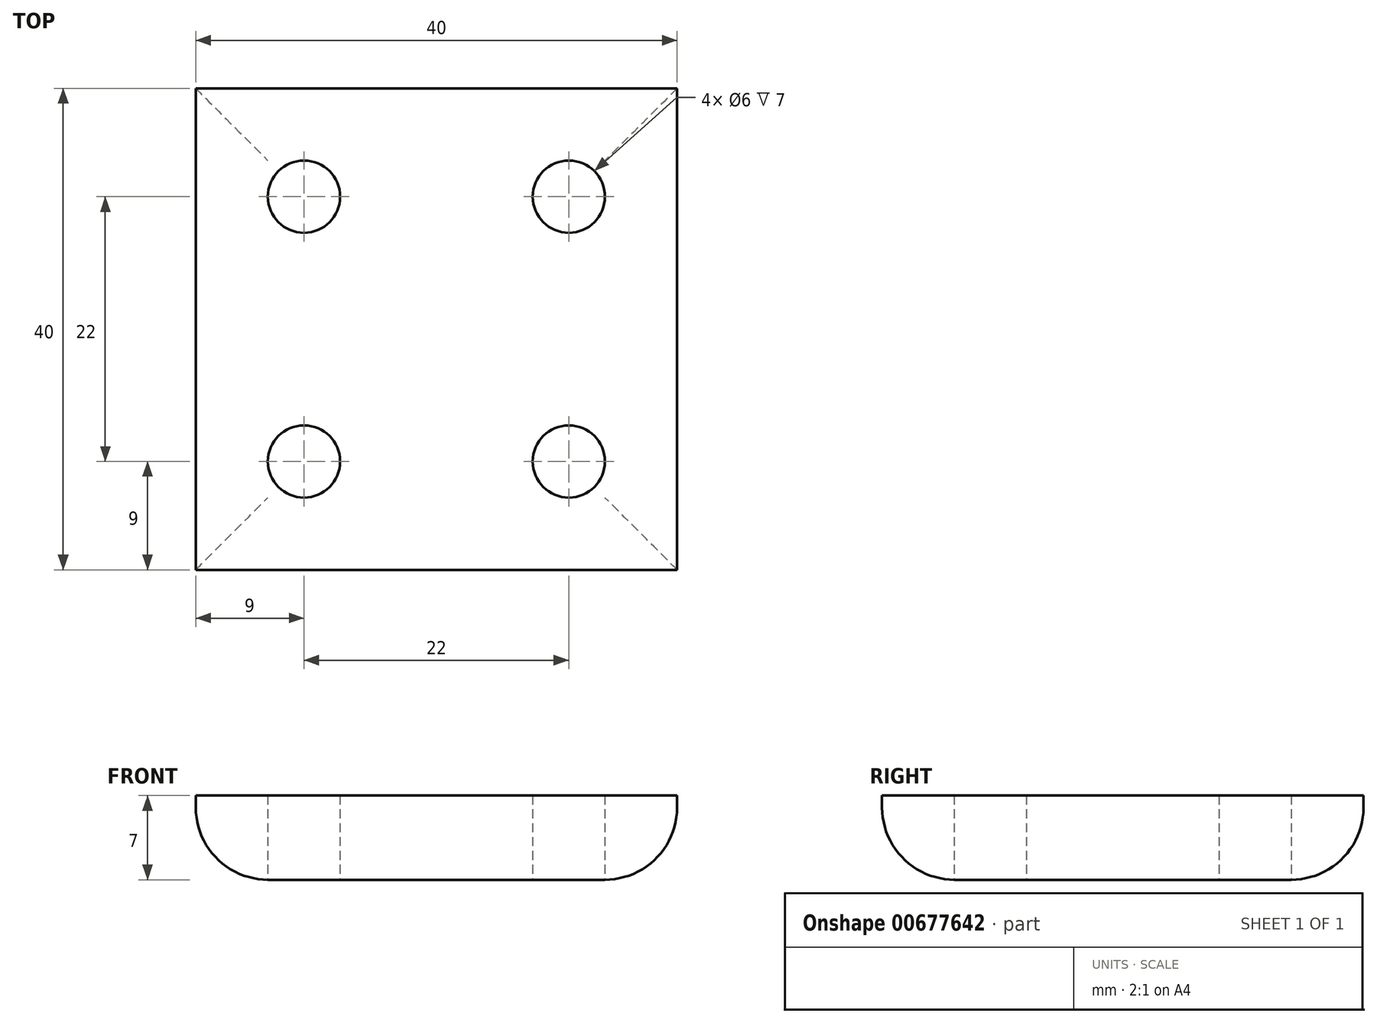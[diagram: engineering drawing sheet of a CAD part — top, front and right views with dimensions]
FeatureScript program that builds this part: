
annotation { "Feature Type Name" : "Feature", "Feature Type Description" : "" }
export const myFeature = defineFeature(function(context is Context, id is Id, definition is map)
    precondition{}
    {
        {
            var Q0;
            Q0=qCreatedBy(makeId("Top.planeOp"),FACE);
            var sketch = newSketch(context, id + "F0", { "sketchPlane" : qUnion([Q0])});
            skLineSegment(sketch, "E0.bottom", {"start": v(0, 0) * mm, "end": v(40, 0) * mm});
            skLineSegment(sketch, "E0.top", {"start": v(0, 40) * mm, "end": v(40, 40) * mm});
            skLineSegment(sketch, "E0.left", {"start": v(0, 0) * mm, "end": v(0, 40) * mm});
            skLineSegment(sketch, "E0.right", {"start": v(40, 0) * mm, "end": v(40, 40) * mm});
            skCircle(sketch, "E1", {"center": v(31, 9) * mm, "radius": 3 * mm});
            skCircle(sketch, "E2.0.1.0", {"center": v(31, 31) * mm, "radius": 3 * mm});
            skCircle(sketch, "E2.1.0.0", {"center": v(9, 9) * mm, "radius": 3 * mm});
            skCircle(sketch, "E2.1.1.0", {"center": v(9, 31) * mm, "radius": 3 * mm});
            skLineSegment(sketch, "E2.direction1", {"start": v(31, 9) * mm, "end": v(9, 9) * mm, "construction": true});
            skLineSegment(sketch, "E2.direction2", {"start": v(31, 9) * mm, "end": v(31, 31) * mm, "construction": true});
            skSolve(sketch);
        }
        {
            var Q0;
            Q0=makeQuery(id+"F0.imprint","IMPRINT",FACE,{"disambiguationData":[TD([[makeQuery(id+"F0.imprint","IMPRINT",EDGE,{"derivedFrom":sQuery(id+"F0.wireOp",EDGE,"E0.bottom")}),1.0]])]});
            extrude(context, id + "F1", {"entities" : qUnion([Q0]), "depth" : 7 * mm, "offsetDistance" : 25 * mm});
        }
        {
            var Q0;
            Q0=makeQuery(id+"F1.opExtrude","CAP_EDGE",EDGE,{"disambiguationData":[OSD([sQuery(id+"F0.wireOp",EDGE,"E0.right")])],"isStart":true});
            var Q1;
            Q1=makeQuery(id+"F1.opExtrude","CAP_EDGE",EDGE,{"disambiguationData":[OSD([sQuery(id+"F0.wireOp",EDGE,"E0.bottom")])],"isStart":true});
            var Q2;
            Q2=makeQuery(id+"F1.opExtrude","CAP_EDGE",EDGE,{"disambiguationData":[OSD([sQuery(id+"F0.wireOp",EDGE,"E0.left")])],"isStart":true});
            var Q3;
            Q3=makeQuery(id+"F1.opExtrude","CAP_EDGE",EDGE,{"disambiguationData":[OSD([sQuery(id+"F0.wireOp",EDGE,"E0.top")])],"isStart":true});
            fillet(context, id + "F2", {"entities" : qUnion([Q0, Q1, Q2, Q3]), "radius" : 6 * mm, "tangentPropagation" : true, "allowEdgeOverflow" : false});
        }
    });
